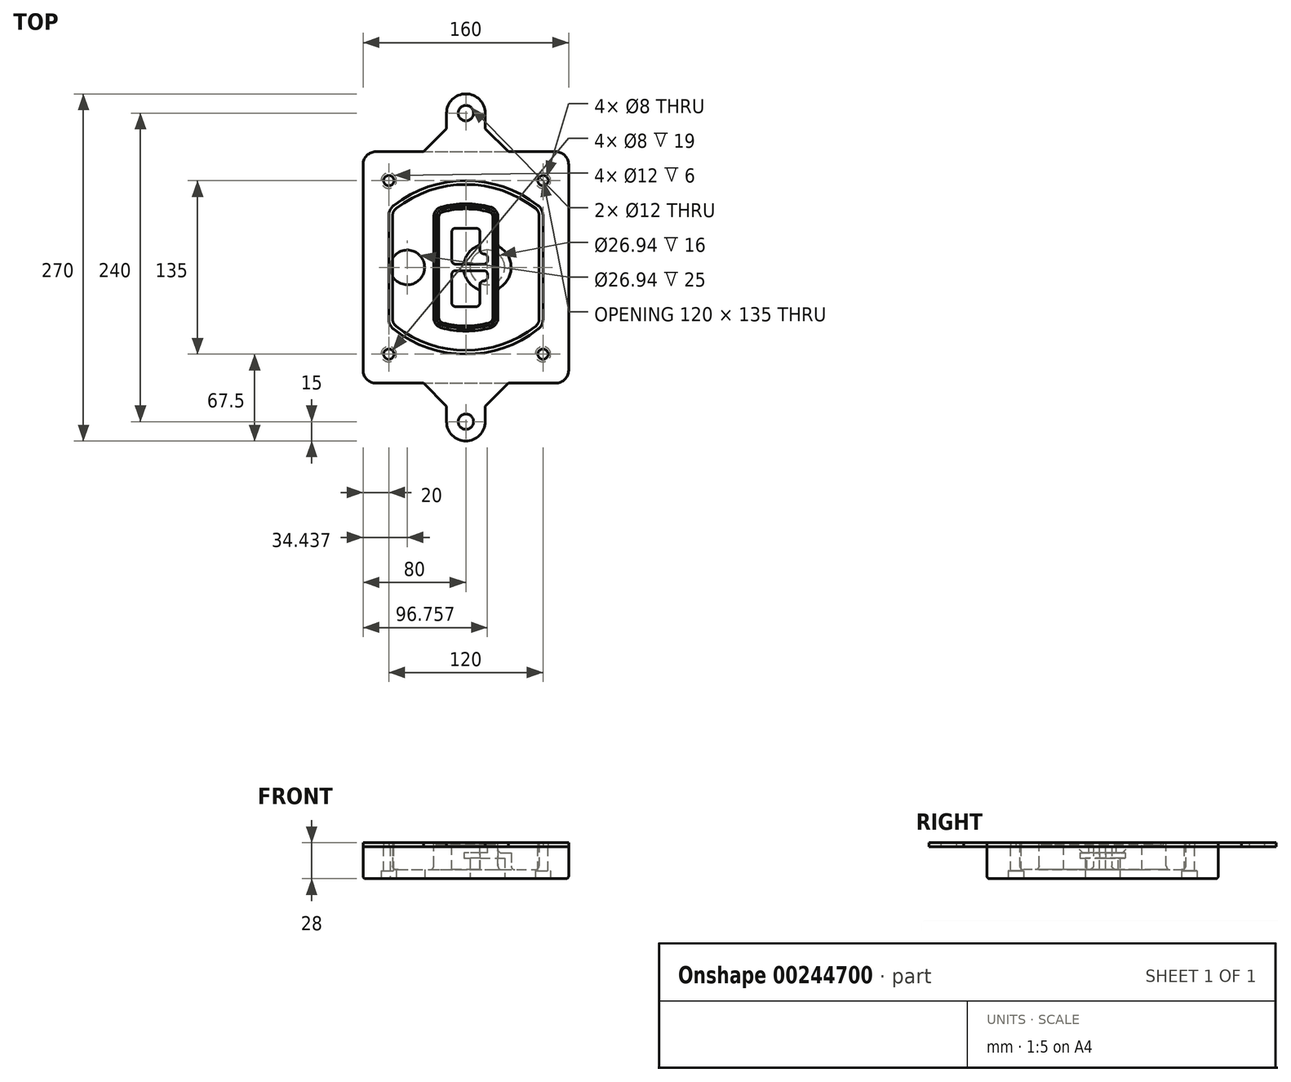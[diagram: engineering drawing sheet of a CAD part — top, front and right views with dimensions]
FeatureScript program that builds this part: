
annotation { "Feature Type Name" : "Feature", "Feature Type Description" : "" }
export const myFeature = defineFeature(function(context is Context, id is Id, definition is map)
    precondition{}
    {
        {
            var Q0;
            Q0=qCreatedBy(makeId("Top.planeOp"),FACE);
            var sketch = newSketch(context, id + "F0", { "sketchPlane" : qUnion([Q0])});
            skPoint(sketch, "E0.rect.middle", {"position": v(0, 0) * mm});
            skLineSegment(sketch, "E1.bottom", {"start": v(-70, -90) * mm, "end": v(70, -90) * mm});
            skLineSegment(sketch, "E1.top", {"start": v(-70, 90) * mm, "end": v(70, 90) * mm});
            skLineSegment(sketch, "E1.left", {"start": v(-80, -80) * mm, "end": v(-80, 80) * mm});
            skLineSegment(sketch, "E1.right", {"start": v(80, -80) * mm, "end": v(80, 80) * mm});
            skLineSegment(sketch, "E2", {"start": v(-80, 90) * mm, "end": v(80, -90) * mm, "construction": true});
            skLineSegment(sketch, "E3", {"start": v(80, 90) * mm, "end": v(-80, -90) * mm, "construction": true});
            skCircle(sketch, "E4", {"center": v(-60, 67.5) * mm, "radius": 4 * mm});
            skCircle(sketch, "E5", {"center": v(60, 67.5) * mm, "radius": 4 * mm});
            skCircle(sketch, "E6", {"center": v(60, -67.5) * mm, "radius": 4 * mm});
            skCircle(sketch, "E7", {"center": v(-60, -67.5) * mm, "radius": 4 * mm});
            skLineSegment(sketch, "E8", {"start": v(-60, 67.5) * mm, "end": v(60, 67.5) * mm, "construction": true});
            skLineSegment(sketch, "E9", {"start": v(60, 67.5) * mm, "end": v(60, -67.5) * mm, "construction": true});
            skLineSegment(sketch, "E10", {"start": v(60, -67.5) * mm, "end": v(-60, -67.5) * mm, "construction": true});
            skLineSegment(sketch, "E11", {"start": v(-60, -67.5) * mm, "end": v(-60, 67.5) * mm, "construction": true});
            skLineSegment(sketch, "E12", {"start": v(-60, 40.3) * mm, "end": v(-60, -40.3) * mm});
            skLineSegment(sketch, "E13", {"start": v(60, 40.3) * mm, "end": v(60, -40.3) * mm});
            skArc(sketch, "E14", {"start": v(56.15, 48.18) * mm, "mid": v(0, 67.5) * mm, "end": v(-56.15, 48.18) * mm});
            skArc(sketch, "E15", {"start": v(-56.15, -48.18) * mm, "mid": v(0, -67.5) * mm, "end": v(56.15, -48.18) * mm});
            skLineSegment(sketch, "E16", {"start": v(-60, 0) * mm, "end": v(60, 0) * mm, "construction": true});
            skPoint(sketch, "E17.visualSharp", {"position": v(-60, -45) * mm});
            skArc(sketch, "E17.filletArc", {"start": v(-60, -40.3) * mm, "mid": v(-58.99, -44.68) * mm, "end": v(-56.15, -48.18) * mm});
            skPoint(sketch, "E18.visualSharp", {"position": v(-60, 45) * mm});
            skArc(sketch, "E18.filletArc", {"start": v(-56.15, 48.18) * mm, "mid": v(-58.99, 44.68) * mm, "end": v(-60, 40.3) * mm});
            skPoint(sketch, "E19.visualSharp", {"position": v(60, 45) * mm});
            skArc(sketch, "E19.filletArc", {"start": v(60, 40.3) * mm, "mid": v(58.99, 44.68) * mm, "end": v(56.15, 48.18) * mm});
            skPoint(sketch, "E20.visualSharp", {"position": v(60, -45) * mm});
            skArc(sketch, "E20.filletArc", {"start": v(56.15, -48.18) * mm, "mid": v(58.99, -44.68) * mm, "end": v(60, -40.3) * mm});
            skPoint(sketch, "E21.visualSharp", {"position": v(-80, 90) * mm});
            skArc(sketch, "E21.filletArc", {"start": v(-70, 90) * mm, "mid": v(-77.07, 87.07) * mm, "end": v(-80, 80) * mm});
            skPoint(sketch, "E22.visualSharp", {"position": v(80, 90) * mm});
            skArc(sketch, "E22.filletArc", {"start": v(80, 80) * mm, "mid": v(77.07, 87.07) * mm, "end": v(70, 90) * mm});
            skPoint(sketch, "E23.visualSharp", {"position": v(80, -90) * mm});
            skArc(sketch, "E23.filletArc", {"start": v(70, -90) * mm, "mid": v(77.07, -87.07) * mm, "end": v(80, -80) * mm});
            skPoint(sketch, "E24.visualSharp", {"position": v(-80, -90) * mm});
            skArc(sketch, "E24.filletArc", {"start": v(-80, -80) * mm, "mid": v(-77.07, -87.07) * mm, "end": v(-70, -90) * mm});
            skArc(sketch, "E25.0", {"start": v(57, 40.3) * mm, "mid": v(56.3, 43.36) * mm, "end": v(54.3, 45.81) * mm});
            skLineSegment(sketch, "E25.1", {"start": v(57, 40.3) * mm, "end": v(57, -40.3) * mm});
            skArc(sketch, "E25.2", {"start": v(54.3, -45.81) * mm, "mid": v(56.3, -43.36) * mm, "end": v(57, -40.3) * mm});
            skArc(sketch, "E25.3", {"start": v(-54.3, -45.81) * mm, "mid": v(0, -64.5) * mm, "end": v(54.3, -45.81) * mm});
            skArc(sketch, "E25.4", {"start": v(-57, -40.3) * mm, "mid": v(-56.3, -43.36) * mm, "end": v(-54.3, -45.81) * mm});
            skArc(sketch, "E25.5", {"start": v(54.3, 45.81) * mm, "mid": v(0, 64.5) * mm, "end": v(-54.3, 45.81) * mm});
            skLineSegment(sketch, "E25.6", {"start": v(-57, 40.3) * mm, "end": v(-57, -40.3) * mm});
            skArc(sketch, "E25.7", {"start": v(-54.3, 45.81) * mm, "mid": v(-56.3, 43.36) * mm, "end": v(-57, 40.3) * mm});
            skArc(sketch, "E26.0", {"start": v(-58.62, 51.33) * mm, "mid": v(-62.58, 46.43) * mm, "end": v(-64, 40.3) * mm});
            skArc(sketch, "E26.1", {"start": v(58.62, 51.33) * mm, "mid": v(0, 71.5) * mm, "end": v(-58.62, 51.33) * mm});
            skArc(sketch, "E26.2", {"start": v(64, 40.3) * mm, "mid": v(62.58, 46.43) * mm, "end": v(58.62, 51.33) * mm});
            skLineSegment(sketch, "E26.3", {"start": v(64, 40.3) * mm, "end": v(64, -40.3) * mm});
            skArc(sketch, "E26.4", {"start": v(58.62, -51.33) * mm, "mid": v(62.58, -46.43) * mm, "end": v(64, -40.3) * mm});
            skLineSegment(sketch, "E26.5", {"start": v(-64, 40.3) * mm, "end": v(-64, -40.3) * mm});
            skArc(sketch, "E26.6", {"start": v(-58.62, -51.33) * mm, "mid": v(0, -71.5) * mm, "end": v(58.62, -51.33) * mm});
            skArc(sketch, "E26.7", {"start": v(-64, -40.3) * mm, "mid": v(-62.58, -46.43) * mm, "end": v(-58.62, -51.33) * mm});
            skSolve(sketch);
        }
        {
            var Q0;
            Q0=makeQuery(id+"F0.imprint","IMPRINT",FACE,{"disambiguationData":[TD([[makeQuery(id+"F0.imprint","IMPRINT",EDGE,{"derivedFrom":sQuery(id+"F0.wireOp",EDGE,"E1.bottom")}),1.0]])]});
            var Q1;
            Q1=makeQuery(id+"F0.imprint","IMPRINT",FACE,{"disambiguationData":[TD([[makeQuery(id+"F0.imprint","IMPRINT",EDGE,{"derivedFrom":sQuery(id+"F0.wireOp",EDGE,"E12")}),1.0]])]});
            var Q2;
            Q2=makeQuery(id+"F0.imprint","IMPRINT",FACE,{"disambiguationData":[TD([[makeQuery(id+"F0.imprint","IMPRINT",EDGE,{"derivedFrom":sQuery(id+"F0.wireOp",EDGE,"E25.0")}),1.0]])]});
            var Q3;
            Q3=makeQuery(id+"F0.imprint","IMPRINT",FACE,{"disambiguationData":[TD([[makeQuery(id+"F0.imprint","IMPRINT",EDGE,{"derivedFrom":sQuery(id+"F0.wireOp",EDGE,"E12")}),-1.0]])]});
            extrude(context, id + "F1", {"entities" : qUnion([Q0, Q1, Q2, Q3]), "oppositeDirection" : true, "depth" : 25 * mm});
        }
        {
            var Q0;
            Q0=makeQuery(id+"F0.imprint","IMPRINT",FACE,{"disambiguationData":[TD([[makeQuery(id+"F0.imprint","IMPRINT",EDGE,{"derivedFrom":sQuery(id+"F0.wireOp",EDGE,"E12")}),1.0]])]});
            extrude(context, id + "F2", {"entities" : qUnion([Q0]), "operationType" : NewBodyOperationType.ADD, "depth" : 3 * mm});
        }
        {
            var Q0;
            Q0=makeQuery(id+"F0.imprint","IMPRINT",FACE,{"disambiguationData":[TD([[makeQuery(id+"F0.imprint","IMPRINT",EDGE,{"derivedFrom":sQuery(id+"F0.wireOp",EDGE,"E25.0")}),1.0]])]});
            extrude(context, id + "F3", {"entities" : qUnion([Q0]), "operationType" : NewBodyOperationType.REMOVE, "oppositeDirection" : true, "depth" : 18 * mm});
        }
        {
            var Q0;
            Q0=makeQuery(id+"F2.opExtrude","CAP_FACE",FACE,{"disambiguationData":[OSD([sQuery(id+"F0.wireOp",EDGE,"E12"),sQuery(id+"F0.wireOp",EDGE,"E13"),sQuery(id+"F0.wireOp",EDGE,"E14"),sQuery(id+"F0.wireOp",EDGE,"E15"),sQuery(id+"F0.wireOp",EDGE,"E17.filletArc"),sQuery(id+"F0.wireOp",EDGE,"E18.filletArc"),sQuery(id+"F0.wireOp",EDGE,"E19.filletArc"),sQuery(id+"F0.wireOp",EDGE,"E20.filletArc"),sQuery(id+"F0.wireOp",EDGE,"E25.0"),sQuery(id+"F0.wireOp",EDGE,"E25.1"),sQuery(id+"F0.wireOp",EDGE,"E25.2"),sQuery(id+"F0.wireOp",EDGE,"E25.3"),sQuery(id+"F0.wireOp",EDGE,"E25.4"),sQuery(id+"F0.wireOp",EDGE,"E25.5"),sQuery(id+"F0.wireOp",EDGE,"E25.6"),sQuery(id+"F0.wireOp",EDGE,"E25.7")])],"isStart":false});
            var sketch = newSketch(context, id + "F4", { "sketchPlane" : qUnion([Q0])});
            skArc(sketch, "E27.0", {"start": v(-19.08, -46.97) * mm, "mid": v(0, -49.5) * mm, "end": v(19.08, -46.97) * mm});
            skArc(sketch, "E28.0", {"start": v(19.08, 46.97) * mm, "mid": v(0, 49.5) * mm, "end": v(-19.08, 46.97) * mm});
            skLineSegment(sketch, "E29", {"start": v(-25, 39.25) * mm, "end": v(-25, -39.25) * mm});
            skLineSegment(sketch, "E30", {"start": v(25, 39.25) * mm, "end": v(25, -39.25) * mm});
            skLineSegment(sketch, "E31", {"start": v(-25, 45.1) * mm, "end": v(25, 45.1) * mm, "construction": true});
            skLineSegment(sketch, "E32", {"start": v(-25, -45.1) * mm, "end": v(25, -45.1) * mm, "construction": true});
            skPoint(sketch, "E33.visualSharp", {"position": v(-25, 45.1) * mm});
            skArc(sketch, "E33.filletArc", {"start": v(-19.08, 46.97) * mm, "mid": v(-23.35, 44.11) * mm, "end": v(-25, 39.25) * mm});
            skPoint(sketch, "E34.visualSharp", {"position": v(25, 45.1) * mm});
            skArc(sketch, "E34.filletArc", {"start": v(25, 39.25) * mm, "mid": v(23.35, 44.11) * mm, "end": v(19.08, 46.97) * mm});
            skPoint(sketch, "E35.visualSharp", {"position": v(25, -45.1) * mm});
            skArc(sketch, "E35.filletArc", {"start": v(19.08, -46.97) * mm, "mid": v(23.35, -44.11) * mm, "end": v(25, -39.25) * mm});
            skPoint(sketch, "E36.visualSharp", {"position": v(-25, -45.1) * mm});
            skArc(sketch, "E36.filletArc", {"start": v(-25, -39.25) * mm, "mid": v(-23.35, -44.11) * mm, "end": v(-19.08, -46.97) * mm});
            skArc(sketch, "E37.0", {"start": v(54.3, 45.81) * mm, "mid": v(0, 64.5) * mm, "end": v(-54.3, 45.81) * mm});
            skArc(sketch, "E37.1", {"start": v(-54.3, 45.81) * mm, "mid": v(-56.3, 43.36) * mm, "end": v(-57, 40.3) * mm});
            skLineSegment(sketch, "E37.2", {"start": v(-57, 40.3) * mm, "end": v(-57, -40.3) * mm});
            skArc(sketch, "E37.3", {"start": v(-57, -40.3) * mm, "mid": v(-56.3, -43.36) * mm, "end": v(-54.3, -45.81) * mm});
            skArc(sketch, "E37.4", {"start": v(-54.3, -45.81) * mm, "mid": v(0, -64.5) * mm, "end": v(54.3, -45.81) * mm});
            skArc(sketch, "E37.5", {"start": v(54.3, -45.81) * mm, "mid": v(56.3, -43.36) * mm, "end": v(57, -40.3) * mm});
            skLineSegment(sketch, "E37.6", {"start": v(57, 40.3) * mm, "end": v(57, -40.3) * mm});
            skArc(sketch, "E37.7", {"start": v(57, 40.3) * mm, "mid": v(56.3, 43.36) * mm, "end": v(54.3, 45.81) * mm});
            skLineSegment(sketch, "E38.0", {"start": v(23, 39.25) * mm, "end": v(23, -39.25) * mm});
            skArc(sketch, "E38.1", {"start": v(18.56, -45.04) * mm, "mid": v(21.76, -42.9) * mm, "end": v(23, -39.25) * mm});
            skArc(sketch, "E38.2", {"start": v(-18.56, -45.04) * mm, "mid": v(0, -47.5) * mm, "end": v(18.56, -45.04) * mm});
            skArc(sketch, "E38.3", {"start": v(-23, -39.25) * mm, "mid": v(-21.76, -42.9) * mm, "end": v(-18.56, -45.04) * mm});
            skLineSegment(sketch, "E38.4", {"start": v(-23, 39.25) * mm, "end": v(-23, -39.25) * mm});
            skArc(sketch, "E38.5", {"start": v(23, 39.25) * mm, "mid": v(21.76, 42.9) * mm, "end": v(18.56, 45.04) * mm});
            skArc(sketch, "E38.6", {"start": v(-18.56, 45.04) * mm, "mid": v(-21.76, 42.9) * mm, "end": v(-23, 39.25) * mm});
            skArc(sketch, "E38.7", {"start": v(18.56, 45.04) * mm, "mid": v(0, 47.5) * mm, "end": v(-18.56, 45.04) * mm});
            skArc(sketch, "E39.0", {"start": v(21, 39.25) * mm, "mid": v(20.18, 41.68) * mm, "end": v(18.04, 43.1) * mm});
            skLineSegment(sketch, "E39.1", {"start": v(21, 39.25) * mm, "end": v(21, -39.25) * mm});
            skArc(sketch, "E39.2", {"start": v(18.04, -43.1) * mm, "mid": v(20.18, -41.68) * mm, "end": v(21, -39.25) * mm});
            skArc(sketch, "E39.3", {"start": v(-18.04, -43.1) * mm, "mid": v(0, -45.5) * mm, "end": v(18.04, -43.1) * mm});
            skArc(sketch, "E39.4", {"start": v(-21, -39.25) * mm, "mid": v(-20.18, -41.68) * mm, "end": v(-18.04, -43.1) * mm});
            skArc(sketch, "E39.5", {"start": v(18.04, 43.1) * mm, "mid": v(0, 45.5) * mm, "end": v(-18.04, 43.1) * mm});
            skLineSegment(sketch, "E39.6", {"start": v(-21, 39.25) * mm, "end": v(-21, -39.25) * mm});
            skArc(sketch, "E39.7", {"start": v(-18.04, 43.1) * mm, "mid": v(-20.18, 41.68) * mm, "end": v(-21, 39.25) * mm});
            skLineSegment(sketch, "E40", {"start": v(-25, 0) * mm, "end": v(25, 0) * mm, "construction": true});
            skLineSegment(sketch, "E41", {"start": v(-11, 5.5) * mm, "end": v(-11, 27.5) * mm});
            skLineSegment(sketch, "E42", {"start": v(-8, 30.5) * mm, "end": v(8, 30.5) * mm});
            skLineSegment(sketch, "E43", {"start": v(11, 27.5) * mm, "end": v(11, 13.5) * mm});
            skLineSegment(sketch, "E44", {"start": v(14, 10.5) * mm, "end": v(14, 10.5) * mm});
            skLineSegment(sketch, "E45", {"start": v(17, 7.5) * mm, "end": v(17, 5.5) * mm});
            skLineSegment(sketch, "E46", {"start": v(14, 2.5) * mm, "end": v(-8, 2.5) * mm});
            skPoint(sketch, "E47.visualSharp", {"position": v(-11, 30.5) * mm});
            skArc(sketch, "E47.filletArc", {"start": v(-8, 30.5) * mm, "mid": v(-10.12, 29.62) * mm, "end": v(-11, 27.5) * mm});
            skPoint(sketch, "E48.visualSharp", {"position": v(11, 30.5) * mm});
            skArc(sketch, "E48.filletArc", {"start": v(11, 27.5) * mm, "mid": v(10.12, 29.62) * mm, "end": v(8, 30.5) * mm});
            skPoint(sketch, "E49.visualSharp", {"position": v(11, 10.5) * mm});
            skArc(sketch, "E49.filletArc", {"start": v(11, 13.5) * mm, "mid": v(11.88, 11.38) * mm, "end": v(14, 10.5) * mm});
            skPoint(sketch, "E50.visualSharp", {"position": v(17, 10.5) * mm});
            skArc(sketch, "E50.filletArc", {"start": v(17, 7.5) * mm, "mid": v(16.12, 9.62) * mm, "end": v(14, 10.5) * mm});
            skPoint(sketch, "E51.visualSharp", {"position": v(17, 2.5) * mm});
            skArc(sketch, "E51.filletArc", {"start": v(14, 2.5) * mm, "mid": v(16.12, 3.38) * mm, "end": v(17, 5.5) * mm});
            skPoint(sketch, "E52.visualSharp", {"position": v(-11, 2.5) * mm});
            skArc(sketch, "E52.filletArc", {"start": v(-11, 5.5) * mm, "mid": v(-10.12, 3.38) * mm, "end": v(-8, 2.5) * mm});
            skLineSegment(sketch, "E53.0.MirrorCS", {"start": v(14, -2.5) * mm, "end": v(-8, -2.5) * mm});
            skArc(sketch, "E54.0.MirrorCS", {"start": v(-11, -5.5) * mm, "mid": v(-10.12, -3.38) * mm, "end": v(-8, -2.5) * mm});
            skLineSegment(sketch, "E55.0.MirrorCS", {"start": v(-11, -5.5) * mm, "end": v(-11, -27.5) * mm});
            skArc(sketch, "E56.0.MirrorCS", {"start": v(-8, -30.5) * mm, "mid": v(-10.12, -29.62) * mm, "end": v(-11, -27.5) * mm});
            skLineSegment(sketch, "E57.0.MirrorCS", {"start": v(-8, -30.5) * mm, "end": v(8, -30.5) * mm});
            skArc(sketch, "E58.0.MirrorCS", {"start": v(11, -27.5) * mm, "mid": v(10.12, -29.62) * mm, "end": v(8, -30.5) * mm});
            skLineSegment(sketch, "E59.0.MirrorCS", {"start": v(11, -27.5) * mm, "end": v(11, -13.5) * mm});
            skArc(sketch, "E60.0.MirrorCS", {"start": v(11, -13.5) * mm, "mid": v(11.88, -11.38) * mm, "end": v(14, -10.5) * mm});
            skArc(sketch, "E61.0.MirrorCS", {"start": v(17, -7.5) * mm, "mid": v(16.12, -9.62) * mm, "end": v(14, -10.5) * mm});
            skLineSegment(sketch, "E62.0.MirrorCS", {"start": v(17, -7.5) * mm, "end": v(17, -5.5) * mm});
            skArc(sketch, "E63.0.MirrorCS", {"start": v(14, -2.5) * mm, "mid": v(16.12, -3.38) * mm, "end": v(17, -5.5) * mm});
            skSolve(sketch);
        }
        {
            var Q0;
            Q0=makeQuery(id+"F4.imprint","IMPRINT",FACE,{"disambiguationData":[TD([[makeQuery(id+"F4.imprint","IMPRINT",EDGE,{"derivedFrom":sQuery(id+"F4.wireOp",EDGE,"E27.0")}),1.0]])]});
            var Q1;
            Q1=makeQuery(id+"F4.imprint","IMPRINT",FACE,{"disambiguationData":[TD([[makeQuery(id+"F4.imprint","IMPRINT",EDGE,{"derivedFrom":sQuery(id+"F4.wireOp",EDGE,"E38.0")}),-1.0]])]});
            var Q2;
            Q2=makeQuery(id+"F4.imprint","IMPRINT",FACE,{"disambiguationData":[TD([[makeQuery(id+"F4.imprint","IMPRINT",EDGE,{"derivedFrom":sQuery(id+"F4.wireOp",EDGE,"E39.0")}),1.0]])]});
            extrude(context, id + "F5", {"entities" : qUnion([Q0, Q1, Q2]), "operationType" : NewBodyOperationType.ADD, "endBound" : BoundingType.UP_TO_NEXT, "oppositeDirection" : true, "depth" : 25 * mm});
        }
        {
            var Q0;
            Q0=makeQuery(id+"F4.imprint","IMPRINT",FACE,{"disambiguationData":[TD([[makeQuery(id+"F4.imprint","IMPRINT",EDGE,{"derivedFrom":sQuery(id+"F4.wireOp",EDGE,"E38.0")}),-1.0]])]});
            extrude(context, id + "F6", {"entities" : qUnion([Q0]), "operationType" : NewBodyOperationType.REMOVE, "oppositeDirection" : true, "depth" : 2 * mm});
        }
        {
            var Q0;
            Q0=makeQuery(id+"F1.opExtrude","CAP_FACE",FACE,{"disambiguationData":[OSD([sQuery(id+"F0.wireOp",EDGE,"E1.bottom"),sQuery(id+"F0.wireOp",EDGE,"E1.top"),sQuery(id+"F0.wireOp",EDGE,"E1.left"),sQuery(id+"F0.wireOp",EDGE,"E1.right"),sQuery(id+"F0.wireOp",EDGE,"E4"),sQuery(id+"F0.wireOp",EDGE,"E5"),sQuery(id+"F0.wireOp",EDGE,"E6"),sQuery(id+"F0.wireOp",EDGE,"E7"),sQuery(id+"F0.wireOp",EDGE,"E21.filletArc"),sQuery(id+"F0.wireOp",EDGE,"E22.filletArc"),sQuery(id+"F0.wireOp",EDGE,"E23.filletArc"),sQuery(id+"F0.wireOp",EDGE,"E24.filletArc")])],"isStart":false});
            var sketch = newSketch(context, id + "F7", { "sketchPlane" : qUnion([Q0])});
            skCircle(sketch, "E64", {"center": v(16.76, 0) * mm, "radius": 13.47 * mm});
            skCircle(sketch, "E65", {"center": v(-45.56, 0) * mm, "radius": 13.47 * mm});
            skLineSegment(sketch, "E66", {"start": v(80, 0) * mm, "end": v(-80, 0) * mm});
            skCircle(sketch, "E67", {"center": v(16.76, 0) * mm, "radius": 18.47 * mm});
            skCircle(sketch, "E68", {"center": v(60, -67.5) * mm, "radius": 6 * mm});
            skCircle(sketch, "E69", {"center": v(-60, -67.5) * mm, "radius": 6 * mm});
            skCircle(sketch, "E70", {"center": v(-60, 67.5) * mm, "radius": 6 * mm});
            skCircle(sketch, "E71", {"center": v(60, 67.5) * mm, "radius": 6 * mm});
            skSolve(sketch);
        }
        {
            var Q0;
            {var subQ1=sQuery(id+"F7.wireOp",EDGE,"E66");var subQ4=sQuery(id+"F7.wireOp",EDGE,"E64");var subQ6=makeQuery(id+"F7.imprint","INTERSECT",VERTEX,{"disambiguationData":[OD(0.0)],"derivedFrom":[subQ4,subQ1]});Q0=makeQuery(id+"F7.imprint","IMPRINT",FACE,{"disambiguationData":[TD([[makeQuery(id+"F7.imprint","IMPRINT",EDGE,{"disambiguationData":[TD([[subQ6,-1.0]])],"derivedFrom":subQ4}),-1.0]])]});}
            var Q1;
            {var subQ0=sQuery(id+"F7.wireOp",EDGE,"E66");var subQ1=sQuery(id+"F7.wireOp",EDGE,"E64");var subQ3=makeQuery(id+"F7.imprint","INTERSECT",VERTEX,{"disambiguationData":[OD(0.0)],"derivedFrom":[subQ1,subQ0]});Q1=makeQuery(id+"F7.imprint","IMPRINT",FACE,{"disambiguationData":[TD([[makeQuery(id+"F7.imprint","IMPRINT",EDGE,{"disambiguationData":[TD([[subQ3,-1.0]])],"derivedFrom":subQ1}),1.0]])]});}
            var Q2;
            {var subQ0=sQuery(id+"F7.wireOp",EDGE,"E66");var subQ1=sQuery(id+"F7.wireOp",EDGE,"E64");var subQ3=makeQuery(id+"F7.imprint","INTERSECT",VERTEX,{"disambiguationData":[OD(0.0)],"derivedFrom":[subQ1,subQ0]});Q2=makeQuery(id+"F7.imprint","IMPRINT",FACE,{"disambiguationData":[TD([[makeQuery(id+"F7.imprint","IMPRINT",EDGE,{"disambiguationData":[TD([[subQ3,1.0]])],"derivedFrom":subQ1}),1.0]])]});}
            var Q3;
            {var subQ1=sQuery(id+"F7.wireOp",EDGE,"E66");var subQ4=sQuery(id+"F7.wireOp",EDGE,"E64");var subQ6=makeQuery(id+"F7.imprint","INTERSECT",VERTEX,{"disambiguationData":[OD(0.0)],"derivedFrom":[subQ4,subQ1]});Q3=makeQuery(id+"F7.imprint","IMPRINT",FACE,{"disambiguationData":[TD([[makeQuery(id+"F7.imprint","IMPRINT",EDGE,{"disambiguationData":[TD([[subQ6,1.0]])],"derivedFrom":subQ4}),-1.0]])]});}
            extrude(context, id + "F8", {"entities" : qUnion([Q0, Q1, Q2, Q3]), "operationType" : NewBodyOperationType.ADD, "oppositeDirection" : true, "depth" : 20 * mm});
        }
        {
            var Q0;
            {var subQ0=sQuery(id+"F7.wireOp",EDGE,"E66");var subQ1=sQuery(id+"F7.wireOp",EDGE,"E64");var subQ3=makeQuery(id+"F7.imprint","INTERSECT",VERTEX,{"disambiguationData":[OD(0.0)],"derivedFrom":[subQ1,subQ0]});Q0=makeQuery(id+"F7.imprint","IMPRINT",FACE,{"disambiguationData":[TD([[makeQuery(id+"F7.imprint","IMPRINT",EDGE,{"disambiguationData":[TD([[subQ3,-1.0]])],"derivedFrom":subQ1}),1.0]])]});}
            var Q1;
            {var subQ0=sQuery(id+"F7.wireOp",EDGE,"E66");var subQ1=sQuery(id+"F7.wireOp",EDGE,"E64");var subQ3=makeQuery(id+"F7.imprint","INTERSECT",VERTEX,{"disambiguationData":[OD(0.0)],"derivedFrom":[subQ1,subQ0]});Q1=makeQuery(id+"F7.imprint","IMPRINT",FACE,{"disambiguationData":[TD([[makeQuery(id+"F7.imprint","IMPRINT",EDGE,{"disambiguationData":[TD([[subQ3,1.0]])],"derivedFrom":subQ1}),1.0]])]});}
            extrude(context, id + "F9", {"entities" : qUnion([Q0, Q1]), "operationType" : NewBodyOperationType.REMOVE, "oppositeDirection" : true, "depth" : 16 * mm});
        }
        {
            var Q0;
            {var subQ0=sQuery(id+"F7.wireOp",EDGE,"E66");var subQ1=sQuery(id+"F7.wireOp",EDGE,"E65");var subQ3=makeQuery(id+"F7.imprint","INTERSECT",VERTEX,{"disambiguationData":[OD(0.0)],"derivedFrom":[subQ1,subQ0]});Q0=makeQuery(id+"F7.imprint","IMPRINT",FACE,{"disambiguationData":[TD([[makeQuery(id+"F7.imprint","IMPRINT",EDGE,{"disambiguationData":[TD([[subQ3,-1.0]])],"derivedFrom":subQ1}),1.0]])]});}
            var Q1;
            {var subQ0=sQuery(id+"F7.wireOp",EDGE,"E66");var subQ1=sQuery(id+"F7.wireOp",EDGE,"E65");var subQ3=makeQuery(id+"F7.imprint","INTERSECT",VERTEX,{"disambiguationData":[OD(0.0)],"derivedFrom":[subQ1,subQ0]});Q1=makeQuery(id+"F7.imprint","IMPRINT",FACE,{"disambiguationData":[TD([[makeQuery(id+"F7.imprint","IMPRINT",EDGE,{"disambiguationData":[TD([[subQ3,1.0]])],"derivedFrom":subQ1}),1.0]])]});}
            extrude(context, id + "F10", {"entities" : qUnion([Q0, Q1]), "operationType" : NewBodyOperationType.REMOVE, "oppositeDirection" : true, "depth" : 25 * mm});
        }
        {
            var Q0;
            Q0=makeQuery(id+"F7.imprint","IMPRINT",FACE,{"disambiguationData":[TD([[makeQuery(id+"F7.imprint","IMPRINT",EDGE,{"derivedFrom":sQuery(id+"F7.wireOp",EDGE,"E68")}),1.0]])]});
            var Q1;
            Q1=makeQuery(id+"F7.imprint","IMPRINT",FACE,{"disambiguationData":[TD([[makeQuery(id+"F7.imprint","IMPRINT",EDGE,{"derivedFrom":makeQuery(id+"F1.opExtrude","CAP_EDGE",EDGE,{"disambiguationData":[OSD([sQuery(id+"F0.wireOp",EDGE,"E5")])],"isStart":false})}),-1.0]])]});
            var Q2;
            Q2=makeQuery(id+"F7.imprint","IMPRINT",FACE,{"disambiguationData":[TD([[makeQuery(id+"F7.imprint","IMPRINT",EDGE,{"derivedFrom":sQuery(id+"F7.wireOp",EDGE,"E69")}),1.0]])]});
            var Q3;
            Q3=makeQuery(id+"F7.imprint","IMPRINT",FACE,{"disambiguationData":[TD([[makeQuery(id+"F7.imprint","IMPRINT",EDGE,{"derivedFrom":makeQuery(id+"F1.opExtrude","CAP_EDGE",EDGE,{"disambiguationData":[OSD([sQuery(id+"F0.wireOp",EDGE,"E4")])],"isStart":false})}),-1.0]])]});
            var Q4;
            Q4=makeQuery(id+"F7.imprint","IMPRINT",FACE,{"disambiguationData":[TD([[makeQuery(id+"F7.imprint","IMPRINT",EDGE,{"derivedFrom":sQuery(id+"F7.wireOp",EDGE,"E70")}),1.0]])]});
            var Q5;
            Q5=makeQuery(id+"F7.imprint","IMPRINT",FACE,{"disambiguationData":[TD([[makeQuery(id+"F7.imprint","IMPRINT",EDGE,{"derivedFrom":makeQuery(id+"F1.opExtrude","CAP_EDGE",EDGE,{"disambiguationData":[OSD([sQuery(id+"F0.wireOp",EDGE,"E7")])],"isStart":false})}),-1.0]])]});
            var Q6;
            Q6=makeQuery(id+"F7.imprint","IMPRINT",FACE,{"disambiguationData":[TD([[makeQuery(id+"F7.imprint","IMPRINT",EDGE,{"derivedFrom":sQuery(id+"F7.wireOp",EDGE,"E71")}),1.0]])]});
            var Q7;
            Q7=makeQuery(id+"F7.imprint","IMPRINT",FACE,{"disambiguationData":[TD([[makeQuery(id+"F7.imprint","IMPRINT",EDGE,{"derivedFrom":makeQuery(id+"F1.opExtrude","CAP_EDGE",EDGE,{"disambiguationData":[OSD([sQuery(id+"F0.wireOp",EDGE,"E6")])],"isStart":false})}),-1.0]])]});
            extrude(context, id + "F11", {"entities" : qUnion([Q0, Q1, Q2, Q3, Q4, Q5, Q6, Q7]), "operationType" : NewBodyOperationType.REMOVE, "oppositeDirection" : true, "depth" : 6 * mm});
        }
        {
            var Q0;
            Q0=makeQuery(id+"F9.boolean.opBoolean","COPY",FACE,{"derivedFrom":makeQuery(id+"F9.opExtrude","CAP_FACE",FACE,{"disambiguationData":[OSD([sQuery(id+"F7.wireOp",EDGE,"E64")])],"isStart":false})});
            var sketch = newSketch(context, id + "F12", { "sketchPlane" : qUnion([Q0])});
            skArc(sketch, "E72.0", {"start": v(11, 17.55) * mm, "mid": v(2.57, 11.82) * mm, "end": v(-1.54, 2.5) * mm});
            skArc(sketch, "E72.1", {"start": v(-1.54, -2.5) * mm, "mid": v(2.57, -11.82) * mm, "end": v(11, -17.55) * mm});
            skLineSegment(sketch, "E73", {"start": v(-1.54, -2.5) * mm, "end": v(14, -2.5) * mm});
            skLineSegment(sketch, "E74.0", {"start": v(14, 2.5) * mm, "end": v(-1.54, 2.5) * mm});
            skArc(sketch, "E74.1", {"start": v(14, 2.5) * mm, "mid": v(16.12, 3.38) * mm, "end": v(17, 5.5) * mm});
            skLineSegment(sketch, "E74.2", {"start": v(17, 7.5) * mm, "end": v(17, 5.5) * mm});
            skArc(sketch, "E74.3", {"start": v(17, 7.5) * mm, "mid": v(16.12, 9.62) * mm, "end": v(14, 10.5) * mm});
            skArc(sketch, "E74.4", {"start": v(11, 13.5) * mm, "mid": v(11.88, 11.38) * mm, "end": v(14, 10.5) * mm});
            skLineSegment(sketch, "E74.5", {"start": v(11, 17.55) * mm, "end": v(11, 13.5) * mm});
            skLineSegment(sketch, "E74.7", {"start": v(14, -2.5) * mm, "end": v(-1.54, -2.5) * mm});
            skArc(sketch, "E74.8", {"start": v(14, -2.5) * mm, "mid": v(16.12, -3.38) * mm, "end": v(17, -5.5) * mm});
            skLineSegment(sketch, "E74.9", {"start": v(17, -7.5) * mm, "end": v(17, -5.5) * mm});
            skArc(sketch, "E74.10", {"start": v(17, -7.5) * mm, "mid": v(16.12, -9.62) * mm, "end": v(14, -10.5) * mm});
            skArc(sketch, "E74.11", {"start": v(11, -13.5) * mm, "mid": v(11.88, -11.38) * mm, "end": v(14, -10.5) * mm});
            skLineSegment(sketch, "E74.12", {"start": v(11, -17.55) * mm, "end": v(11, -13.5) * mm});
            skPoint(sketch, "E75.orphan", {"position": v(11, -27.5) * mm});
            skPoint(sketch, "E76.orphan", {"position": v(-8, -2.5) * mm});
            skPoint(sketch, "E77.orphan", {"position": v(-8, 2.5) * mm});
            skPoint(sketch, "E78.orphan", {"position": v(11, 27.5) * mm});
            skSolve(sketch);
        }
        {
            var Q0;
            {var subQ7=sQuery(id+"F12.wireOp",EDGE,"E72.0");var subQ14=sQuery(id+"F12.wireOp",EDGE,"E72.1");var subQ16=sQuery(id+"F12.wireOp",EDGE,"E74.1");var subQ18=sQuery(id+"F12.wireOp",EDGE,"E74.8");Q0=qUnion([makeQuery(id+"F12.imprint","IMPRINT",FACE,{"disambiguationData":[TD([[makeQuery(id+"F12.imprint","IMPRINT",EDGE,{"derivedFrom":subQ7}),1.0]])]}),makeQuery(id+"F12.imprint","IMPRINT",FACE,{"disambiguationData":[TD([[makeQuery(id+"F12.imprint","IMPRINT",EDGE,{"derivedFrom":subQ14}),1.0]])]}),makeQuery(id+"F12.imprint","IMPRINT",FACE,{"disambiguationData":[TD([[makeQuery(id+"F12.imprint","IMPRINT",EDGE,{"derivedFrom":subQ16}),1.0]])]}),makeQuery(id+"F12.imprint","IMPRINT",FACE,{"disambiguationData":[TD([[makeQuery(id+"F12.imprint","IMPRINT",EDGE,{"derivedFrom":subQ18}),-1.0]])]})]);}
            var Q1;
            Q1=makeQuery(id+"F5.boolean.opBoolean","SPLIT",FACE,{"disambiguationData":[TD([makeQuery(id+"F5.opExtrude","SWEPT_FACE",FACE,{"disambiguationData":[OSD([sQuery(id+"F4.wireOp",EDGE,"E41")])]})])],"derivedFrom":makeQuery(id+"F3.boolean.opBoolean","COPY",FACE,{"derivedFrom":makeQuery(id+"F3.opExtrude","CAP_FACE",FACE,{"disambiguationData":[OSD([sQuery(id+"F0.wireOp",EDGE,"E25.0"),sQuery(id+"F0.wireOp",EDGE,"E25.1"),sQuery(id+"F0.wireOp",EDGE,"E25.2"),sQuery(id+"F0.wireOp",EDGE,"E25.3"),sQuery(id+"F0.wireOp",EDGE,"E25.4"),sQuery(id+"F0.wireOp",EDGE,"E25.5"),sQuery(id+"F0.wireOp",EDGE,"E25.6"),sQuery(id+"F0.wireOp",EDGE,"E25.7")])],"isStart":false})})});
            extrude(context, id + "F13", {"entities" : qUnion([Q0]), "operationType" : NewBodyOperationType.REMOVE, "endBound" : BoundingType.UP_TO_SURFACE, "endBoundEntityFace" : qUnion([Q1]), "depth" : 25 * mm});
        }
        {
            var Q0;
            Q0=makeQuery(id+"F3.boolean.opBoolean","COPY",EDGE,{"derivedFrom":makeQuery(id+"F3.opExtrude","CAP_EDGE",EDGE,{"disambiguationData":[OSD([sQuery(id+"F0.wireOp",EDGE,"E25.6")])],"isStart":false})});
            var Q1;
            Q1=makeQuery(id+"F8.boolean.opBoolean","INTERSECT",EDGE,{"derivedFrom":[makeQuery(id+"F5.opExtrude","SWEPT_FACE",FACE,{"disambiguationData":[OSD([sQuery(id+"F4.wireOp",EDGE,"E30")])]}),makeQuery(id+"F8.opExtrude","CAP_FACE",FACE,{"disambiguationData":[OSD([sQuery(id+"F7.wireOp",EDGE,"E67")])],"isStart":false})]});
            var Q2;
            Q2=makeQuery(id+"F8.boolean.opBoolean","INTERSECT",EDGE,{"disambiguationData":[OD(1.0)],"derivedFrom":[makeQuery(id+"F5.opExtrude","SWEPT_FACE",FACE,{"disambiguationData":[OSD([sQuery(id+"F4.wireOp",EDGE,"E30")])]}),makeQuery(id+"F8.opExtrude","SWEPT_FACE",FACE,{"disambiguationData":[OSD([sQuery(id+"F7.wireOp",EDGE,"E67")])]})]});
            var Q3;
            {var subQ0=sQuery(id+"F4.wireOp",EDGE,"E30");Q3=makeQuery(id+"F8.boolean.opBoolean","SPLIT",EDGE,{"disambiguationData":[TD([makeQuery(id+"F5.opExtrude","SWEPT_FACE",FACE,{"disambiguationData":[OSD([sQuery(id+"F4.wireOp",EDGE,"E35.filletArc")])]})])],"derivedFrom":makeQuery(id+"F5.opExtrude","CAP_EDGE",EDGE,{"disambiguationData":[OSD([subQ0])],"isStart":false})});}
            var Q4;
            {var subQ0=sQuery(id+"F0.wireOp",EDGE,"E25.7");var subQ1=sQuery(id+"F0.wireOp",EDGE,"E25.1");var subQ2=sQuery(id+"F0.wireOp",EDGE,"E25.6");var subQ3=sQuery(id+"F0.wireOp",EDGE,"E25.5");var subQ4=sQuery(id+"F0.wireOp",EDGE,"E25.4");var subQ5=sQuery(id+"F0.wireOp",EDGE,"E25.0");var subQ6=sQuery(id+"F0.wireOp",EDGE,"E25.2");var subQ7=sQuery(id+"F0.wireOp",EDGE,"E25.3");Q4=makeQuery(id+"F8.boolean.opBoolean","INTERSECT",EDGE,{"derivedFrom":[makeQuery(id+"F5.boolean.opBoolean","SPLIT",FACE,{"disambiguationData":[TD([makeQuery(id+"F2.opExtrude","SWEPT_FACE",FACE,{"disambiguationData":[OSD([subQ5])]})])],"derivedFrom":makeQuery(id+"F3.boolean.opBoolean","COPY",FACE,{"derivedFrom":makeQuery(id+"F3.opExtrude","CAP_FACE",FACE,{"disambiguationData":[OSD([subQ5,subQ1,subQ6,subQ7,subQ4,subQ3,subQ2,subQ0])],"isStart":false})})}),makeQuery(id+"F8.opExtrude","SWEPT_FACE",FACE,{"disambiguationData":[OSD([sQuery(id+"F7.wireOp",EDGE,"E67")])]})]});}
            var Q5;
            Q5=makeQuery(id+"F8.boolean.opBoolean","INTERSECT",EDGE,{"disambiguationData":[OD(0.0)],"derivedFrom":[makeQuery(id+"F5.opExtrude","SWEPT_FACE",FACE,{"disambiguationData":[OSD([sQuery(id+"F4.wireOp",EDGE,"E30")])]}),makeQuery(id+"F8.opExtrude","SWEPT_FACE",FACE,{"disambiguationData":[OSD([sQuery(id+"F7.wireOp",EDGE,"E67")])]})]});
            fillet(context, id + "F14", {"entities" : qUnion([Q0, Q1, Q2, Q3, Q4, Q5]), "radius" : 3 * mm, "tangentPropagation" : true, "allowEdgeOverflow" : false});
        }
        {
            var Q0;
            Q0=makeQuery(id+"F1.opExtrude","CAP_EDGE",EDGE,{"disambiguationData":[OSD([sQuery(id+"F0.wireOp",EDGE,"E1.bottom")])],"isStart":false});
            fillet(context, id + "F15", {"entities" : qUnion([Q0]), "radius" : 2 * mm, "tangentPropagation" : true, "allowEdgeOverflow" : false});
        }
        {
            var Q0;
            {var subQ0=sQuery(id+"F0.wireOp",EDGE,"E22.filletArc");var subQ1=sQuery(id+"F0.wireOp",EDGE,"E7");var subQ2=sQuery(id+"F0.wireOp",EDGE,"E6");var subQ3=sQuery(id+"F0.wireOp",EDGE,"E5");var subQ4=sQuery(id+"F0.wireOp",EDGE,"E4");var subQ5=sQuery(id+"F0.wireOp",EDGE,"E1.bottom");var subQ6=sQuery(id+"F0.wireOp",EDGE,"E21.filletArc");var subQ7=sQuery(id+"F0.wireOp",EDGE,"E1.top");var subQ8=sQuery(id+"F0.wireOp",EDGE,"E1.left");var subQ9=sQuery(id+"F0.wireOp",EDGE,"E1.right");var subQ10=sQuery(id+"F0.wireOp",EDGE,"E23.filletArc");var subQ11=sQuery(id+"F0.wireOp",EDGE,"E24.filletArc");Q0=makeQuery(id+"F2.boolean.opBoolean","SPLIT",FACE,{"disambiguationData":[TD([makeQuery(id+"F1.opExtrude","SWEPT_FACE",FACE,{"disambiguationData":[OSD([subQ5])]})])],"derivedFrom":makeQuery(id+"F1.opExtrude","CAP_FACE",FACE,{"disambiguationData":[OSD([subQ5,subQ7,subQ8,subQ9,subQ4,subQ3,subQ2,subQ1,subQ6,subQ0,subQ10,subQ11])],"isStart":true})});}
            var sketch = newSketch(context, id + "F16", { "sketchPlane" : qUnion([Q0])});
            skLineSegment(sketch, "E79", {"start": v(0, 90) * mm, "end": v(0, 120) * mm, "construction": true});
            skLineSegment(sketch, "E80", {"start": v(-33, 90) * mm, "end": v(-15, 108) * mm});
            skLineSegment(sketch, "E81", {"start": v(-15, 108) * mm, "end": v(-15, 120) * mm});
            skLineSegment(sketch, "E82", {"start": v(33, 90) * mm, "end": v(15, 108) * mm});
            skLineSegment(sketch, "E83", {"start": v(15, 108) * mm, "end": v(15, 120) * mm});
            skCircle(sketch, "E84", {"center": v(0, 120) * mm, "radius": 6 * mm});
            skArc(sketch, "E85", {"start": v(15, 120) * mm, "mid": v(0, 135) * mm, "end": v(-15, 120) * mm});
            skLineSegment(sketch, "E86", {"start": v(0, 0) * mm, "end": v(108.47, 0) * mm, "construction": true});
            skLineSegment(sketch, "E87.MirrorCS", {"start": v(0, -90) * mm, "end": v(0, -120) * mm, "construction": true});
            skLineSegment(sketch, "E88.MirrorCS", {"start": v(-33, -90) * mm, "end": v(-15, -108) * mm});
            skLineSegment(sketch, "E89.MirrorCS", {"start": v(-15, -108) * mm, "end": v(-15, -120) * mm});
            skLineSegment(sketch, "E90.MirrorCS", {"start": v(33, -90) * mm, "end": v(15, -108) * mm});
            skLineSegment(sketch, "E91.MirrorCS", {"start": v(15, -108) * mm, "end": v(15, -120) * mm});
            skCircle(sketch, "E92.MirrorC", {"center": v(0, -120) * mm, "radius": 6 * mm});
            skArc(sketch, "E93.MirrorCS", {"start": v(15, -120) * mm, "mid": v(0, -135) * mm, "end": v(-15, -120) * mm});
            skSolve(sketch);
        }
        {
            var Q0;
            {var subQ1=sQuery(id+"F16.wireOp",EDGE,"E80");Q0=makeQuery(id+"F16.imprint","IMPRINT",FACE,{"disambiguationData":[TD([[makeQuery(id+"F16.imprint","IMPRINT",EDGE,{"derivedFrom":subQ1}),-1.0]])]});}
            var Q1;
            Q1=makeQuery(id+"F16.imprint","IMPRINT",FACE,{"disambiguationData":[TD([[makeQuery(id+"F16.imprint","IMPRINT",EDGE,{"derivedFrom":makeQuery(id+"F1.opExtrude","CAP_EDGE",EDGE,{"disambiguationData":[OSD([sQuery(id+"F0.wireOp",EDGE,"E1.left")])],"isStart":true})}),-1.0]])]});
            var Q2;
            {var subQ1=sQuery(id+"F16.wireOp",EDGE,"E88.MirrorCS");Q2=makeQuery(id+"F16.imprint","IMPRINT",FACE,{"disambiguationData":[TD([[makeQuery(id+"F16.imprint","IMPRINT",EDGE,{"derivedFrom":subQ1}),1.0]])]});}
            var Q3;
            Q3=makeQuery(id+"F2.opExtrude","CAP_FACE",FACE,{"disambiguationData":[OSD([sQuery(id+"F0.wireOp",EDGE,"E12"),sQuery(id+"F0.wireOp",EDGE,"E13"),sQuery(id+"F0.wireOp",EDGE,"E14"),sQuery(id+"F0.wireOp",EDGE,"E15"),sQuery(id+"F0.wireOp",EDGE,"E17.filletArc"),sQuery(id+"F0.wireOp",EDGE,"E18.filletArc"),sQuery(id+"F0.wireOp",EDGE,"E19.filletArc"),sQuery(id+"F0.wireOp",EDGE,"E20.filletArc"),sQuery(id+"F0.wireOp",EDGE,"E25.0"),sQuery(id+"F0.wireOp",EDGE,"E25.1"),sQuery(id+"F0.wireOp",EDGE,"E25.2"),sQuery(id+"F0.wireOp",EDGE,"E25.3"),sQuery(id+"F0.wireOp",EDGE,"E25.4"),sQuery(id+"F0.wireOp",EDGE,"E25.5"),sQuery(id+"F0.wireOp",EDGE,"E25.6"),sQuery(id+"F0.wireOp",EDGE,"E25.7")])],"isStart":false});
            extrude(context, id + "F17", {"entities" : qUnion([Q0, Q1, Q2]), "endBound" : BoundingType.UP_TO_SURFACE, "endBoundEntityFace" : qUnion([Q3]), "depth" : 25 * mm});
        }
    });
